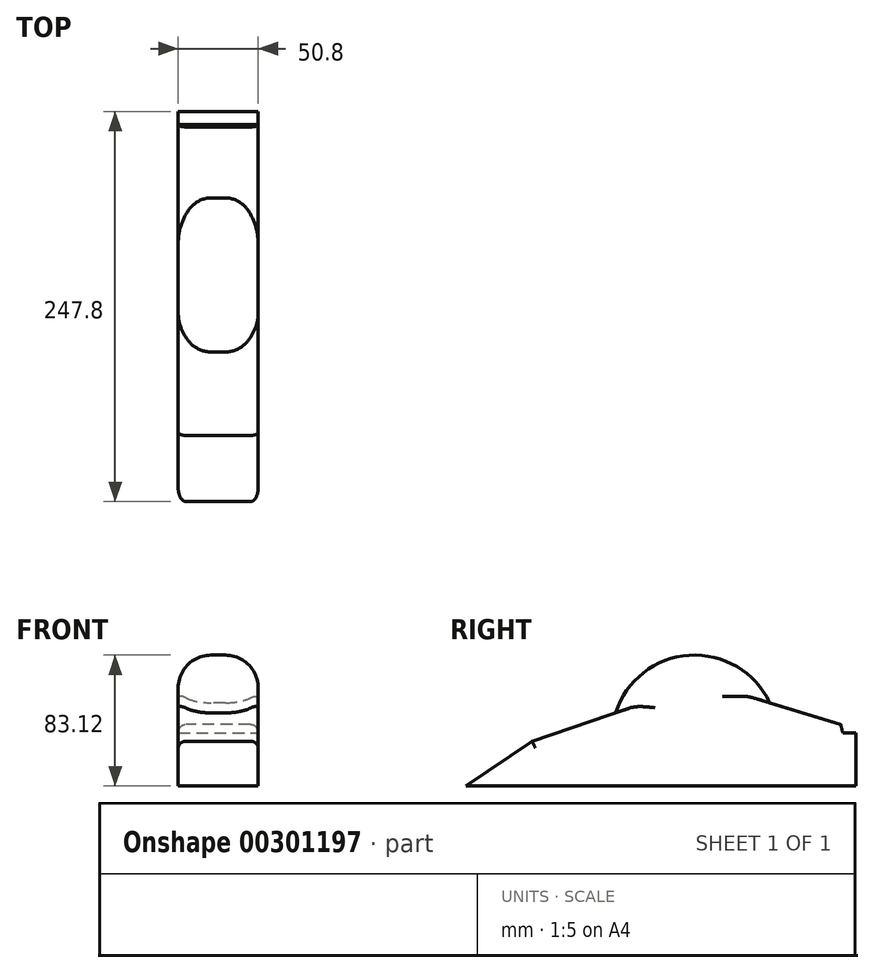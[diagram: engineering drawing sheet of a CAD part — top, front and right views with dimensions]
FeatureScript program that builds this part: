
annotation { "Feature Type Name" : "Feature", "Feature Type Description" : "" }
export const myFeature = defineFeature(function(context is Context, id is Id, definition is map)
    precondition{}
    {
        {
            var Q0;
            Q0=qCreatedBy(makeId("Right.planeOp"),FACE);
            var sketch = newSketch(context, id + "F0", { "sketchPlane" : qUnion([Q0])});
            skLineSegment(sketch, "E0", {"start": v(0, 0) * mm, "end": v(-146, 0) * mm});
            skLineSegment(sketch, "E1", {"start": v(-146, 0) * mm, "end": v(-103.94, 28.5) * mm});
            skLineSegment(sketch, "E2", {"start": v(-103.94, 28.5) * mm, "end": v(-50.9, 46.48) * mm});
            skLineSegment(sketch, "E3", {"start": v(-50.9, 46.48) * mm, "end": v(0, 52.88) * mm});
            skLineSegment(sketch, "E4", {"start": v(0, 52.88) * mm, "end": v(46.94, 52.88) * mm});
            skLineSegment(sketch, "E5", {"start": v(46.94, 52.88) * mm, "end": v(92.05, 39.17) * mm});
            skLineSegment(sketch, "E6", {"start": v(92.05, 39.17) * mm, "end": v(101.8, 0) * mm});
            skLineSegment(sketch, "E7", {"start": v(101.8, 0) * mm, "end": v(0, 0) * mm});
            skArc(sketch, "E8", {"start": v(46.94, 52.88) * mm, "mid": v(-4.16, 83.01) * mm, "end": v(-50.9, 46.48) * mm});
            skSolve(sketch);
        }
        {
            var Q0;
            Q0 = qSketchRegion(id + "F0", true);
            extrude(context, id + "F1", {"entities" : qUnion([Q0]), "depth" : 50.8 * mm});
        }
        {
            var Q0;
            Q0=makeQuery(id+"F1.opExtrude","CAP_EDGE",EDGE,{"disambiguationData":[OSD([sQuery(id+"F0.wireOp",EDGE,"E2")])],"isStart":false});
            var Q1;
            Q1=makeQuery(id+"F1.opExtrude","CAP_EDGE",EDGE,{"disambiguationData":[OSD([sQuery(id+"F0.wireOp",EDGE,"E1")])],"isStart":false});
            var Q2;
            Q2=makeQuery(id+"F1.opExtrude","CAP_EDGE",EDGE,{"disambiguationData":[OSD([sQuery(id+"F0.wireOp",EDGE,"E1")])],"isStart":true});
            var Q3;
            Q3=makeQuery(id+"F1.opExtrude","CAP_EDGE",EDGE,{"disambiguationData":[OSD([sQuery(id+"F0.wireOp",EDGE,"E2")])],"isStart":true});
            var Q4;
            Q4=makeQuery(id+"F1.opExtrude","CAP_EDGE",EDGE,{"disambiguationData":[OSD([sQuery(id+"F0.wireOp",EDGE,"E5")])],"isStart":false});
            var Q5;
            Q5=makeQuery(id+"F1.opExtrude","CAP_EDGE",EDGE,{"disambiguationData":[OSD([sQuery(id+"F0.wireOp",EDGE,"E5")])],"isStart":true});
            fillet(context, id + "F2", {"entities" : qUnion([Q0, Q1, Q2, Q3, Q4, Q5]), "radius" : 4.9 * mm, "tangentPropagation" : true, "allowEdgeOverflow" : false});
        }
        {
            var Q0;
            Q0=makeQuery(id+"F1.opExtrude","CAP_EDGE",EDGE,{"disambiguationData":[OSD([sQuery(id+"F0.wireOp",EDGE,"E8")])],"isStart":true});
            var Q1;
            Q1=makeQuery(id+"F1.opExtrude","CAP_EDGE",EDGE,{"disambiguationData":[OSD([sQuery(id+"F0.wireOp",EDGE,"E8")])],"isStart":false});
            fillet(context, id + "F3", {"entities" : qUnion([Q0, Q1]), "radius" : 20.85 * mm, "tangentPropagation" : true, "allowEdgeOverflow" : false});
        }
        {
            var Q0;
            Q0=makeQuery(id+"F1.opExtrude","CAP_FACE",FACE,{"disambiguationData":[OSD([sQuery(id+"F0.wireOp",EDGE,"E0"),sQuery(id+"F0.wireOp",EDGE,"E1"),sQuery(id+"F0.wireOp",EDGE,"E2"),sQuery(id+"F0.wireOp",EDGE,"E5"),sQuery(id+"F0.wireOp",EDGE,"E6"),sQuery(id+"F0.wireOp",EDGE,"E7"),sQuery(id+"F0.wireOp",EDGE,"E8")])],"isStart":false});
            var sketch = newSketch(context, id + "F4", { "sketchPlane" : qUnion([Q0])});
            skLineSegment(sketch, "E9", {"start": v(101.8, 0) * mm, "end": v(101.8, 33.62) * mm});
            skLineSegment(sketch, "E10", {"start": v(101.8, 33.62) * mm, "end": v(93.43, 33.62) * mm});
            skSolve(sketch);
        }
        {
            var Q0;
            Q0=makeQuery(id+"F4.imprint","IMPRINT",FACE,{"disambiguationData":[TD([[makeQuery(id+"F4.imprint","IMPRINT",EDGE,{"derivedFrom":sQuery(id+"F4.wireOp",EDGE,"E9")}),1.0]])]});
            extrude(context, id + "F5", {"entities" : qUnion([Q0]), "operationType" : NewBodyOperationType.ADD, "oppositeDirection" : true, "depth" : 50.8 * mm});
        }
    });
